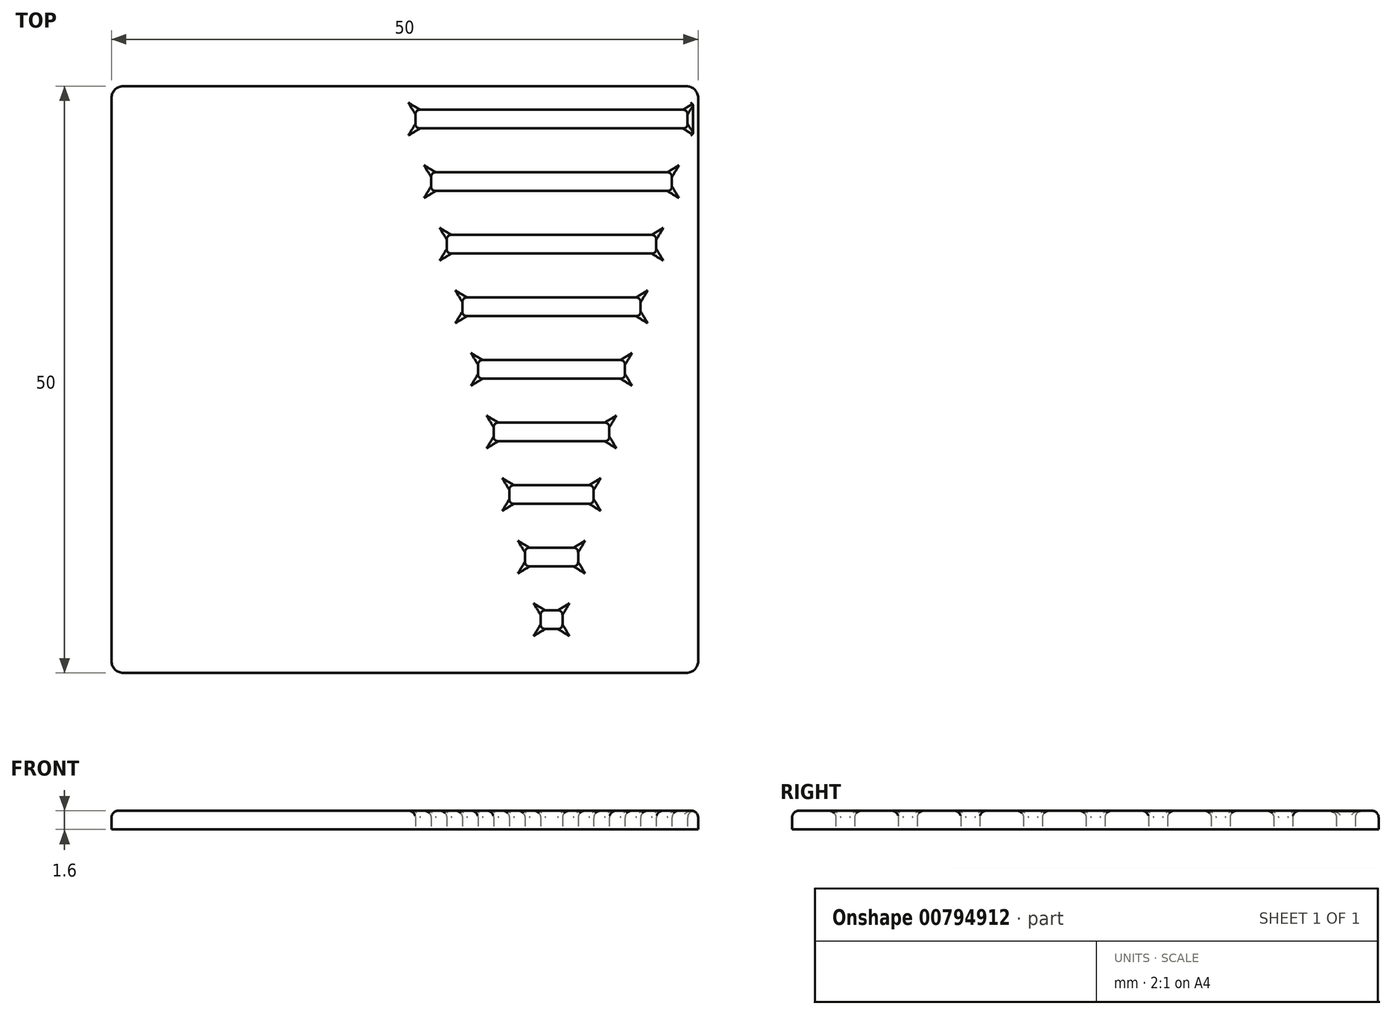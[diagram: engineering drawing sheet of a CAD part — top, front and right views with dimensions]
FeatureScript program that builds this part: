
annotation { "Feature Type Name" : "Feature", "Feature Type Description" : "" }
export const myFeature = defineFeature(function(context is Context, id is Id, definition is map)
    precondition{}
    {
        {
            var Q0;
            Q0=qCreatedBy(makeId("Top.planeOp"),FACE);
            var sketch = newSketch(context, id + "F0", { "sketchPlane" : qUnion([Q0])});
            skLineSegment(sketch, "E0.bottom", {"start": v(-25, 25) * mm, "end": v(25, 25) * mm});
            skLineSegment(sketch, "E0.top", {"start": v(-25, -25) * mm, "end": v(25, -25) * mm});
            skLineSegment(sketch, "E0.left", {"start": v(-25, 25) * mm, "end": v(-25, -25) * mm});
            skLineSegment(sketch, "E0.right", {"start": v(25, 25) * mm, "end": v(25, -25) * mm});
            skLineSegment(sketch, "E1", {"start": v(-25, 25) * mm, "end": v(25, -25) * mm, "construction": true});
            skLineSegment(sketch, "E2", {"start": v(0, 25) * mm, "end": v(0, -25) * mm, "construction": true});
            skLineSegment(sketch, "E3", {"start": v(0, 25) * mm, "end": v(12.5, -25) * mm, "construction": true});
            skLineSegment(sketch, "E4", {"start": v(12.5, -25) * mm, "end": v(25, 25) * mm, "construction": true});
            skLineSegment(sketch, "E5.bottom", {"start": v(11.57, -21.27) * mm, "end": v(13.43, -21.27) * mm});
            skLineSegment(sketch, "E5.top", {"start": v(11.57, -19.67) * mm, "end": v(13.43, -19.67) * mm});
            skLineSegment(sketch, "E5.left", {"start": v(11.57, -21.27) * mm, "end": v(11.57, -19.67) * mm});
            skLineSegment(sketch, "E5.right", {"start": v(13.43, -21.27) * mm, "end": v(13.43, -19.67) * mm});
            skLineSegment(sketch, "E6.bottom", {"start": v(8.9, -10.6) * mm, "end": v(16.1, -10.6) * mm});
            skLineSegment(sketch, "E6.top", {"start": v(8.9, -9) * mm, "end": v(16.1, -9) * mm});
            skLineSegment(sketch, "E6.left", {"start": v(8.9, -10.6) * mm, "end": v(8.9, -9) * mm});
            skLineSegment(sketch, "E6.right", {"start": v(16.1, -10.6) * mm, "end": v(16.1, -9) * mm});
            skLineSegment(sketch, "E7.bottom", {"start": v(10.23, -15.93) * mm, "end": v(14.77, -15.93) * mm});
            skLineSegment(sketch, "E7.top", {"start": v(10.23, -14.33) * mm, "end": v(14.77, -14.33) * mm});
            skLineSegment(sketch, "E7.left", {"start": v(10.23, -15.93) * mm, "end": v(10.23, -14.33) * mm});
            skLineSegment(sketch, "E7.right", {"start": v(14.77, -15.93) * mm, "end": v(14.77, -14.33) * mm});
            skLineSegment(sketch, "E8", {"start": v(11.57, -25) * mm, "end": v(11.57, -21.27) * mm, "construction": true});
            skLineSegment(sketch, "E9", {"start": v(11.57, -19.67) * mm, "end": v(11.57, -15.93) * mm, "construction": true});
            skLineSegment(sketch, "E10", {"start": v(10.23, -14.33) * mm, "end": v(10.23, -10.6) * mm, "construction": true});
            skLineSegment(sketch, "E11.bottom", {"start": v(7.57, -5.27) * mm, "end": v(17.43, -5.27) * mm});
            skLineSegment(sketch, "E11.top", {"start": v(7.57, -3.67) * mm, "end": v(17.43, -3.67) * mm});
            skLineSegment(sketch, "E11.left", {"start": v(7.57, -5.27) * mm, "end": v(7.57, -3.67) * mm});
            skLineSegment(sketch, "E11.right", {"start": v(17.43, -5.27) * mm, "end": v(17.43, -3.67) * mm});
            skLineSegment(sketch, "E12", {"start": v(8.9, -9) * mm, "end": v(8.9, -5.27) * mm, "construction": true});
            skLineSegment(sketch, "E13.bottom", {"start": v(6.23, 0.07) * mm, "end": v(18.77, 0.07) * mm});
            skLineSegment(sketch, "E13.top", {"start": v(6.23, 1.67) * mm, "end": v(18.77, 1.67) * mm});
            skLineSegment(sketch, "E13.left", {"start": v(6.23, 0.07) * mm, "end": v(6.23, 1.67) * mm});
            skLineSegment(sketch, "E13.right", {"start": v(18.77, 0.07) * mm, "end": v(18.77, 1.67) * mm});
            skLineSegment(sketch, "E14", {"start": v(7.57, -3.67) * mm, "end": v(7.57, 0.07) * mm, "construction": true});
            skLineSegment(sketch, "E15.bottom", {"start": v(4.9, 5.4) * mm, "end": v(20.1, 5.4) * mm});
            skLineSegment(sketch, "E15.top", {"start": v(4.9, 7) * mm, "end": v(20.1, 7) * mm});
            skLineSegment(sketch, "E15.left", {"start": v(4.9, 5.4) * mm, "end": v(4.9, 7) * mm});
            skLineSegment(sketch, "E15.right", {"start": v(20.1, 5.4) * mm, "end": v(20.1, 7) * mm});
            skLineSegment(sketch, "E16.bottom", {"start": v(3.57, 10.73) * mm, "end": v(21.43, 10.73) * mm});
            skLineSegment(sketch, "E16.top", {"start": v(3.57, 12.33) * mm, "end": v(21.43, 12.33) * mm});
            skLineSegment(sketch, "E16.left", {"start": v(3.57, 10.73) * mm, "end": v(3.57, 12.33) * mm});
            skLineSegment(sketch, "E16.right", {"start": v(21.43, 10.73) * mm, "end": v(21.43, 12.33) * mm});
            skLineSegment(sketch, "E17.bottom", {"start": v(2.23, 16.07) * mm, "end": v(22.77, 16.07) * mm});
            skLineSegment(sketch, "E17.top", {"start": v(2.23, 17.67) * mm, "end": v(22.77, 17.67) * mm});
            skLineSegment(sketch, "E17.left", {"start": v(2.23, 16.07) * mm, "end": v(2.23, 17.67) * mm});
            skLineSegment(sketch, "E17.right", {"start": v(22.77, 16.07) * mm, "end": v(22.77, 17.67) * mm});
            skLineSegment(sketch, "E18.bottom", {"start": v(0.9, 21.4) * mm, "end": v(24.1, 21.4) * mm});
            skLineSegment(sketch, "E18.top", {"start": v(0.9, 23) * mm, "end": v(24.1, 23) * mm});
            skLineSegment(sketch, "E18.left", {"start": v(0.9, 21.4) * mm, "end": v(0.9, 23) * mm});
            skLineSegment(sketch, "E18.right", {"start": v(24.1, 21.4) * mm, "end": v(24.1, 23) * mm});
            skLineSegment(sketch, "E19", {"start": v(6.23, 1.67) * mm, "end": v(6.23, 5.4) * mm, "construction": true});
            skLineSegment(sketch, "E20", {"start": v(4.9, 7) * mm, "end": v(4.9, 10.73) * mm, "construction": true});
            skLineSegment(sketch, "E21", {"start": v(3.57, 12.33) * mm, "end": v(3.57, 16.07) * mm, "construction": true});
            skLineSegment(sketch, "E22", {"start": v(2.23, 17.67) * mm, "end": v(2.23, 21.4) * mm, "construction": true});
            skLineSegment(sketch, "E23", {"start": v(0.9, 23) * mm, "end": v(0.9, 25) * mm, "construction": true});
            skSolve(sketch);
        }
        {
            var Q0;
            Q0=makeQuery(id+"F0.imprint","IMPRINT",FACE,{"disambiguationData":[TD([[makeQuery(id+"F0.imprint","IMPRINT",EDGE,{"derivedFrom":sQuery(id+"F0.wireOp",EDGE,"E0.bottom")}),-1.0]])]});
            extrude(context, id + "F1", {"entities" : qUnion([Q0]), "depth" : 1.6 * mm, "offsetDistance" : 25 * mm});
        }
        {
            var Q0;
            Q0=makeQuery(id+"F1.opExtrude","CAP_FACE",FACE,{"disambiguationData":[OSD([sQuery(id+"F0.wireOp",EDGE,"E0.bottom"),sQuery(id+"F0.wireOp",EDGE,"E0.top"),sQuery(id+"F0.wireOp",EDGE,"E0.left"),sQuery(id+"F0.wireOp",EDGE,"E0.right"),sQuery(id+"F0.wireOp",EDGE,"E5.bottom"),sQuery(id+"F0.wireOp",EDGE,"E5.top"),sQuery(id+"F0.wireOp",EDGE,"E5.left"),sQuery(id+"F0.wireOp",EDGE,"E5.right"),sQuery(id+"F0.wireOp",EDGE,"E6.bottom"),sQuery(id+"F0.wireOp",EDGE,"E6.top"),sQuery(id+"F0.wireOp",EDGE,"E6.left"),sQuery(id+"F0.wireOp",EDGE,"E6.right"),sQuery(id+"F0.wireOp",EDGE,"E7.bottom"),sQuery(id+"F0.wireOp",EDGE,"E7.top"),sQuery(id+"F0.wireOp",EDGE,"E7.left"),sQuery(id+"F0.wireOp",EDGE,"E7.right"),sQuery(id+"F0.wireOp",EDGE,"E11.bottom"),sQuery(id+"F0.wireOp",EDGE,"E11.top"),sQuery(id+"F0.wireOp",EDGE,"E11.left"),sQuery(id+"F0.wireOp",EDGE,"E11.right"),sQuery(id+"F0.wireOp",EDGE,"E13.bottom"),sQuery(id+"F0.wireOp",EDGE,"E13.top"),sQuery(id+"F0.wireOp",EDGE,"E13.left"),sQuery(id+"F0.wireOp",EDGE,"E13.right")])],"isStart":false});
            fillet(context, id + "F2", {"entities" : qUnion([Q0]), "radius" : 0.6 * mm, "tangentPropagation" : true, "allowEdgeOverflow" : false});
        }
        {
            var Q0;
            Q0=makeQuery(id+"F1.opExtrude","SWEPT_EDGE",EDGE,{"disambiguationData":[OSD([sQuery(id+"F0.wireOp",EDGE,"E11.bottom"),sQuery(id+"F0.wireOp",EDGE,"E11.right")])]});
            var Q1;
            Q1=makeQuery(id+"F1.opExtrude","SWEPT_EDGE",EDGE,{"disambiguationData":[OSD([sQuery(id+"F0.wireOp",EDGE,"E6.bottom"),sQuery(id+"F0.wireOp",EDGE,"E6.right")])]});
            var Q2;
            Q2=makeQuery(id+"F1.opExtrude","SWEPT_EDGE",EDGE,{"disambiguationData":[OSD([sQuery(id+"F0.wireOp",EDGE,"E7.bottom"),sQuery(id+"F0.wireOp",EDGE,"E7.right")])]});
            var Q3;
            Q3=makeQuery(id+"F1.opExtrude","SWEPT_EDGE",EDGE,{"disambiguationData":[OSD([sQuery(id+"F0.wireOp",EDGE,"E5.bottom"),sQuery(id+"F0.wireOp",EDGE,"E5.right")])]});
            var Q4;
            Q4=makeQuery(id+"F1.opExtrude","SWEPT_EDGE",EDGE,{"disambiguationData":[OSD([sQuery(id+"F0.wireOp",EDGE,"E7.top"),sQuery(id+"F0.wireOp",EDGE,"E7.right")])]});
            var Q5;
            Q5=makeQuery(id+"F1.opExtrude","SWEPT_EDGE",EDGE,{"disambiguationData":[OSD([sQuery(id+"F0.wireOp",EDGE,"E6.top"),sQuery(id+"F0.wireOp",EDGE,"E6.right")])]});
            var Q6;
            Q6=makeQuery(id+"F1.opExtrude","SWEPT_EDGE",EDGE,{"disambiguationData":[OSD([sQuery(id+"F0.wireOp",EDGE,"E11.top"),sQuery(id+"F0.wireOp",EDGE,"E11.right")])]});
            var Q7;
            Q7=makeQuery(id+"F1.opExtrude","SWEPT_EDGE",EDGE,{"disambiguationData":[OSD([sQuery(id+"F0.wireOp",EDGE,"E13.top"),sQuery(id+"F0.wireOp",EDGE,"E13.right")])]});
            var Q8;
            Q8=makeQuery(id+"F1.opExtrude","SWEPT_EDGE",EDGE,{"disambiguationData":[OSD([sQuery(id+"F0.wireOp",EDGE,"E5.top"),sQuery(id+"F0.wireOp",EDGE,"E5.right")])]});
            var Q9;
            Q9=makeQuery(id+"F1.opExtrude","SWEPT_EDGE",EDGE,{"disambiguationData":[OSD([sQuery(id+"F0.wireOp",EDGE,"E13.top"),sQuery(id+"F0.wireOp",EDGE,"E13.left")])]});
            var Q10;
            Q10=makeQuery(id+"F1.opExtrude","SWEPT_EDGE",EDGE,{"disambiguationData":[OSD([sQuery(id+"F0.wireOp",EDGE,"E11.top"),sQuery(id+"F0.wireOp",EDGE,"E11.left")])]});
            var Q11;
            Q11=makeQuery(id+"F1.opExtrude","SWEPT_EDGE",EDGE,{"disambiguationData":[OSD([sQuery(id+"F0.wireOp",EDGE,"E6.top"),sQuery(id+"F0.wireOp",EDGE,"E6.left")])]});
            var Q12;
            Q12=makeQuery(id+"F1.opExtrude","SWEPT_EDGE",EDGE,{"disambiguationData":[OSD([sQuery(id+"F0.wireOp",EDGE,"E7.top"),sQuery(id+"F0.wireOp",EDGE,"E7.left")])]});
            var Q13;
            Q13=makeQuery(id+"F1.opExtrude","SWEPT_EDGE",EDGE,{"disambiguationData":[OSD([sQuery(id+"F0.wireOp",EDGE,"E5.top"),sQuery(id+"F0.wireOp",EDGE,"E5.left")])]});
            var Q14;
            Q14=makeQuery(id+"F1.opExtrude","SWEPT_EDGE",EDGE,{"disambiguationData":[OSD([sQuery(id+"F0.wireOp",EDGE,"E7.bottom"),sQuery(id+"F0.wireOp",EDGE,"E7.left")])]});
            var Q15;
            Q15=makeQuery(id+"F1.opExtrude","SWEPT_EDGE",EDGE,{"disambiguationData":[OSD([sQuery(id+"F0.wireOp",EDGE,"E6.bottom"),sQuery(id+"F0.wireOp",EDGE,"E6.left")])]});
            var Q16;
            Q16=makeQuery(id+"F1.opExtrude","SWEPT_EDGE",EDGE,{"disambiguationData":[OSD([sQuery(id+"F0.wireOp",EDGE,"E11.bottom"),sQuery(id+"F0.wireOp",EDGE,"E11.left")])]});
            var Q17;
            Q17=makeQuery(id+"F1.opExtrude","SWEPT_EDGE",EDGE,{"disambiguationData":[OSD([sQuery(id+"F0.wireOp",EDGE,"E13.bottom"),sQuery(id+"F0.wireOp",EDGE,"E13.left")])]});
            var Q18;
            Q18=makeQuery(id+"F1.opExtrude","SWEPT_EDGE",EDGE,{"disambiguationData":[OSD([sQuery(id+"F0.wireOp",EDGE,"E5.bottom"),sQuery(id+"F0.wireOp",EDGE,"E5.left")])]});
            var Q19;
            Q19=makeQuery(id+"F1.opExtrude","SWEPT_EDGE",EDGE,{"disambiguationData":[OSD([sQuery(id+"F0.wireOp",EDGE,"E13.bottom"),sQuery(id+"F0.wireOp",EDGE,"E13.right")])]});
            var Q20;
            Q20=makeQuery(id+"F1.opExtrude","SWEPT_EDGE",EDGE,{"disambiguationData":[OSD([sQuery(id+"F0.wireOp",EDGE,"E15.bottom"),sQuery(id+"F0.wireOp",EDGE,"E15.right")])]});
            var Q21;
            Q21=makeQuery(id+"F1.opExtrude","SWEPT_EDGE",EDGE,{"disambiguationData":[OSD([sQuery(id+"F0.wireOp",EDGE,"E15.top"),sQuery(id+"F0.wireOp",EDGE,"E15.right")])]});
            var Q22;
            Q22=makeQuery(id+"F1.opExtrude","SWEPT_EDGE",EDGE,{"disambiguationData":[OSD([sQuery(id+"F0.wireOp",EDGE,"E17.top"),sQuery(id+"F0.wireOp",EDGE,"E17.right")])]});
            var Q23;
            Q23=makeQuery(id+"F1.opExtrude","SWEPT_EDGE",EDGE,{"disambiguationData":[OSD([sQuery(id+"F0.wireOp",EDGE,"E17.bottom"),sQuery(id+"F0.wireOp",EDGE,"E17.right")])]});
            var Q24;
            Q24=makeQuery(id+"F1.opExtrude","SWEPT_EDGE",EDGE,{"disambiguationData":[OSD([sQuery(id+"F0.wireOp",EDGE,"E16.bottom"),sQuery(id+"F0.wireOp",EDGE,"E16.right")])]});
            var Q25;
            Q25=makeQuery(id+"F1.opExtrude","SWEPT_EDGE",EDGE,{"disambiguationData":[OSD([sQuery(id+"F0.wireOp",EDGE,"E16.top"),sQuery(id+"F0.wireOp",EDGE,"E16.right")])]});
            var Q26;
            Q26=makeQuery(id+"F1.opExtrude","SWEPT_EDGE",EDGE,{"disambiguationData":[OSD([sQuery(id+"F0.wireOp",EDGE,"E18.top"),sQuery(id+"F0.wireOp",EDGE,"E18.right")])]});
            var Q27;
            Q27=makeQuery(id+"F1.opExtrude","SWEPT_EDGE",EDGE,{"disambiguationData":[OSD([sQuery(id+"F0.wireOp",EDGE,"E18.bottom"),sQuery(id+"F0.wireOp",EDGE,"E18.right")])]});
            var Q28;
            Q28=makeQuery(id+"F1.opExtrude","SWEPT_EDGE",EDGE,{"disambiguationData":[OSD([sQuery(id+"F0.wireOp",EDGE,"E18.top"),sQuery(id+"F0.wireOp",EDGE,"E18.left")])]});
            var Q29;
            Q29=makeQuery(id+"F1.opExtrude","SWEPT_EDGE",EDGE,{"disambiguationData":[OSD([sQuery(id+"F0.wireOp",EDGE,"E18.bottom"),sQuery(id+"F0.wireOp",EDGE,"E18.left")])]});
            var Q30;
            Q30=makeQuery(id+"F1.opExtrude","SWEPT_EDGE",EDGE,{"disambiguationData":[OSD([sQuery(id+"F0.wireOp",EDGE,"E17.bottom"),sQuery(id+"F0.wireOp",EDGE,"E17.left")])]});
            var Q31;
            Q31=makeQuery(id+"F1.opExtrude","SWEPT_EDGE",EDGE,{"disambiguationData":[OSD([sQuery(id+"F0.wireOp",EDGE,"E16.bottom"),sQuery(id+"F0.wireOp",EDGE,"E16.left")])]});
            var Q32;
            Q32=makeQuery(id+"F1.opExtrude","SWEPT_EDGE",EDGE,{"disambiguationData":[OSD([sQuery(id+"F0.wireOp",EDGE,"E16.top"),sQuery(id+"F0.wireOp",EDGE,"E16.left")])]});
            var Q33;
            Q33=makeQuery(id+"F1.opExtrude","SWEPT_EDGE",EDGE,{"disambiguationData":[OSD([sQuery(id+"F0.wireOp",EDGE,"E17.top"),sQuery(id+"F0.wireOp",EDGE,"E17.left")])]});
            var Q34;
            Q34=makeQuery(id+"F1.opExtrude","SWEPT_EDGE",EDGE,{"disambiguationData":[OSD([sQuery(id+"F0.wireOp",EDGE,"E15.top"),sQuery(id+"F0.wireOp",EDGE,"E15.left")])]});
            var Q35;
            Q35=makeQuery(id+"F1.opExtrude","SWEPT_EDGE",EDGE,{"disambiguationData":[OSD([sQuery(id+"F0.wireOp",EDGE,"E15.bottom"),sQuery(id+"F0.wireOp",EDGE,"E15.left")])]});
            fillet(context, id + "F3", {"entities" : qUnion([Q0, Q1, Q2, Q3, Q4, Q5, Q6, Q7, Q8, Q9, Q10, Q11, Q12, Q13, Q14, Q15, Q16, Q17, Q18, Q19, Q20, Q21, Q22, Q23, Q24, Q25, Q26, Q27, Q28, Q29, Q30, Q31, Q32, Q33, Q34, Q35]), "radius" : 0.4 * mm, "tangentPropagation" : true, "allowEdgeOverflow" : false});
        }
        {
            var Q0;
            Q0=makeQuery(id+"F1.opExtrude","SWEPT_EDGE",EDGE,{"disambiguationData":[OSD([sQuery(id+"F0.wireOp",EDGE,"E0.bottom"),sQuery(id+"F0.wireOp",EDGE,"E0.right")])]});
            var Q1;
            Q1=makeQuery(id+"F1.opExtrude","SWEPT_EDGE",EDGE,{"disambiguationData":[OSD([sQuery(id+"F0.wireOp",EDGE,"E0.top"),sQuery(id+"F0.wireOp",EDGE,"E0.right")])]});
            var Q2;
            Q2=makeQuery(id+"F1.opExtrude","SWEPT_EDGE",EDGE,{"disambiguationData":[OSD([sQuery(id+"F0.wireOp",EDGE,"E0.top"),sQuery(id+"F0.wireOp",EDGE,"E0.left")])]});
            var Q3;
            Q3=makeQuery(id+"F1.opExtrude","SWEPT_EDGE",EDGE,{"disambiguationData":[OSD([sQuery(id+"F0.wireOp",EDGE,"E0.bottom"),sQuery(id+"F0.wireOp",EDGE,"E0.left")])]});
            fillet(context, id + "F4", {"entities" : qUnion([Q0, Q1, Q2, Q3]), "radius" : 1 * mm, "tangentPropagation" : true, "allowEdgeOverflow" : false});
        }
    });
